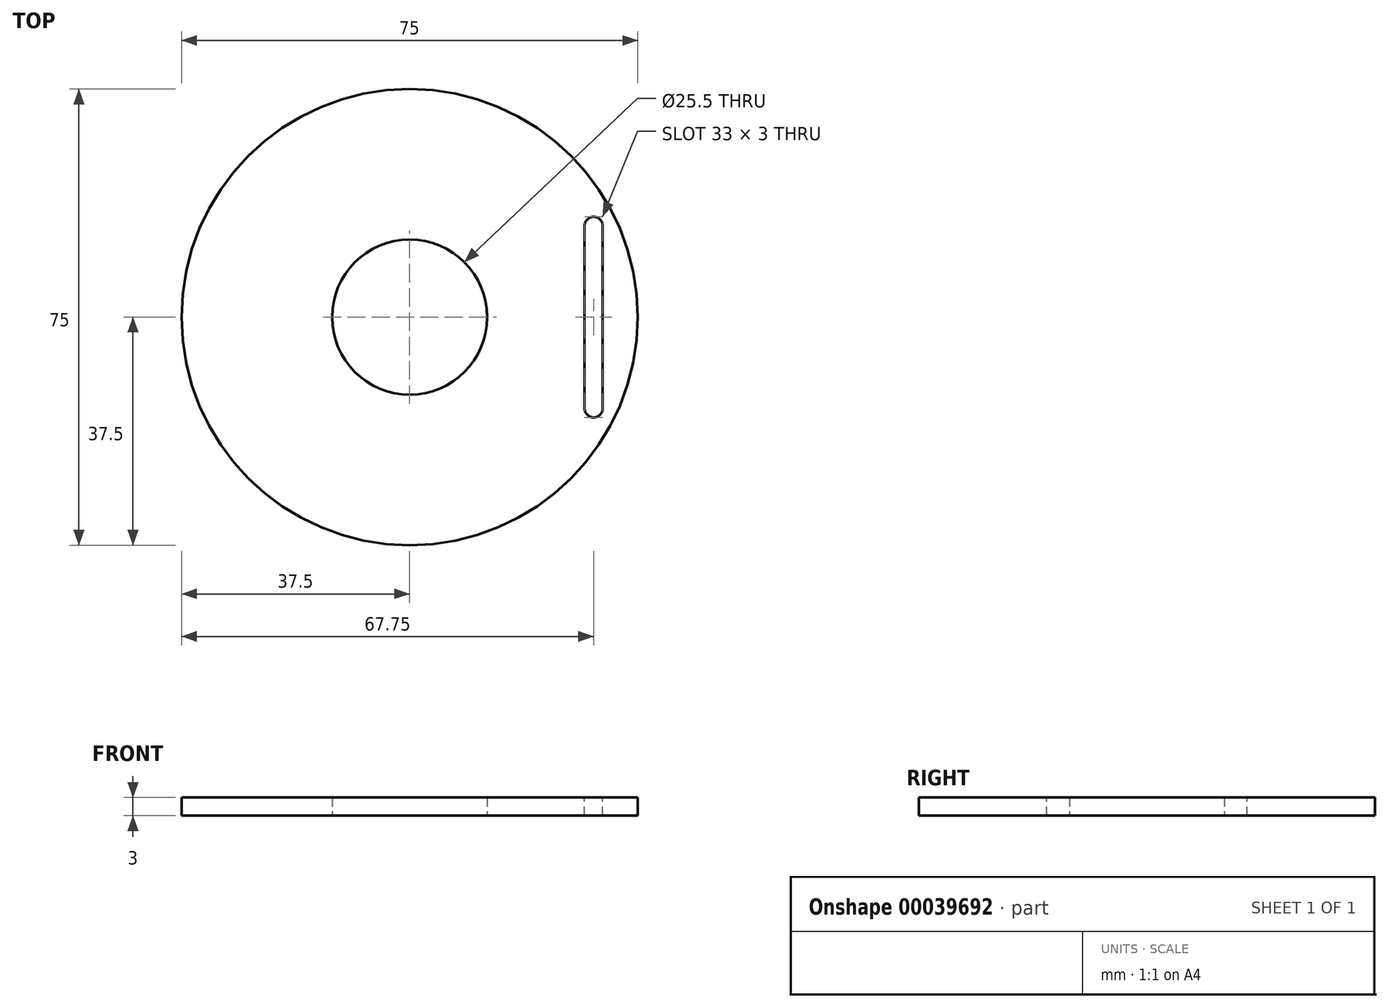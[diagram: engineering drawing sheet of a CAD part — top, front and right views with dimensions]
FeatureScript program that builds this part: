
annotation { "Feature Type Name" : "Feature", "Feature Type Description" : "" }
export const myFeature = defineFeature(function(context is Context, id is Id, definition is map)
    precondition{}
    {
        {
            var Q0;
            Q0=qCreatedBy(makeId("Top.planeOp"),FACE);
            var sketch = newSketch(context, id + "F0", { "sketchPlane" : qUnion([Q0])});
            skCircle(sketch, "E0", {"center": v(0, 0) * mm, "radius": 12.75 * mm});
            skCircle(sketch, "E1", {"center": v(0, 0) * mm, "radius": 37.5 * mm});
            skSolve(sketch);
        }
        {
            var Q0;
            Q0=makeQuery(id+"F0.imprint","IMPRINT",FACE,{"disambiguationData":[TD([[makeQuery(id+"F0.imprint","IMPRINT",EDGE,{"derivedFrom":sQuery(id+"F0.wireOp",EDGE,"facb660d-88cc-4eaf-a54c-0a480d32b3a8")}),-1.0]])]});
            var Q1;
            Q1=makeQuery(id+"F0.imprint","IMPRINT",FACE,{"disambiguationData":[TD([[makeQuery(id+"F0.imprint","IMPRINT",EDGE,{"derivedFrom":sQuery(id+"F0.wireOp",EDGE,"E0")}),-1.0]])]});
            extrude(context, id + "F1", {"entities" : qUnion([Q0, Q1]), "depth" : 3 * mm});
        }
        {
            var Q0;
            Q0=makeQuery(id+"F1.opExtrude","CAP_FACE",FACE,{"disambiguationData":[OSD([sQuery(id+"F0.wireOp",EDGE,"E0"),sQuery(id+"F0.wireOp",EDGE,"E1")])],"isStart":false});
            var sketch = newSketch(context, id + "F2", { "sketchPlane" : qUnion([Q0])});
            skPoint(sketch, "E2", {"position": v(30.25, 15) * mm});
            skPoint(sketch, "E3.MirrorP", {"position": v(30.25, -15) * mm});
            skArc(sketch, "E4", {"start": v(31.75, 15) * mm, "mid": v(30.25, 16.5) * mm, "end": v(28.75, 15) * mm});
            skArc(sketch, "E5", {"start": v(28.75, -15) * mm, "mid": v(30.25, -16.5) * mm, "end": v(31.75, -15) * mm});
            skLineSegment(sketch, "E6", {"start": v(31.75, 15) * mm, "end": v(31.75, -15) * mm});
            skLineSegment(sketch, "E7", {"start": v(28.75, 15) * mm, "end": v(28.75, -15) * mm});
            skSolve(sketch);
        }
        {
            var Q0;
            Q0=makeQuery(id+"F2.imprint","IMPRINT",FACE,{"disambiguationData":[TD([[makeQuery(id+"F2.imprint","IMPRINT",EDGE,{"derivedFrom":sQuery(id+"F2.wireOp",EDGE,"E4")}),1.0]])]});
            extrude(context, id + "F3", {"entities" : qUnion([Q0]), "operationType" : NewBodyOperationType.REMOVE, "endBound" : BoundingType.UP_TO_NEXT, "oppositeDirection" : true, "depth" : 25 * mm});
        }
    });
